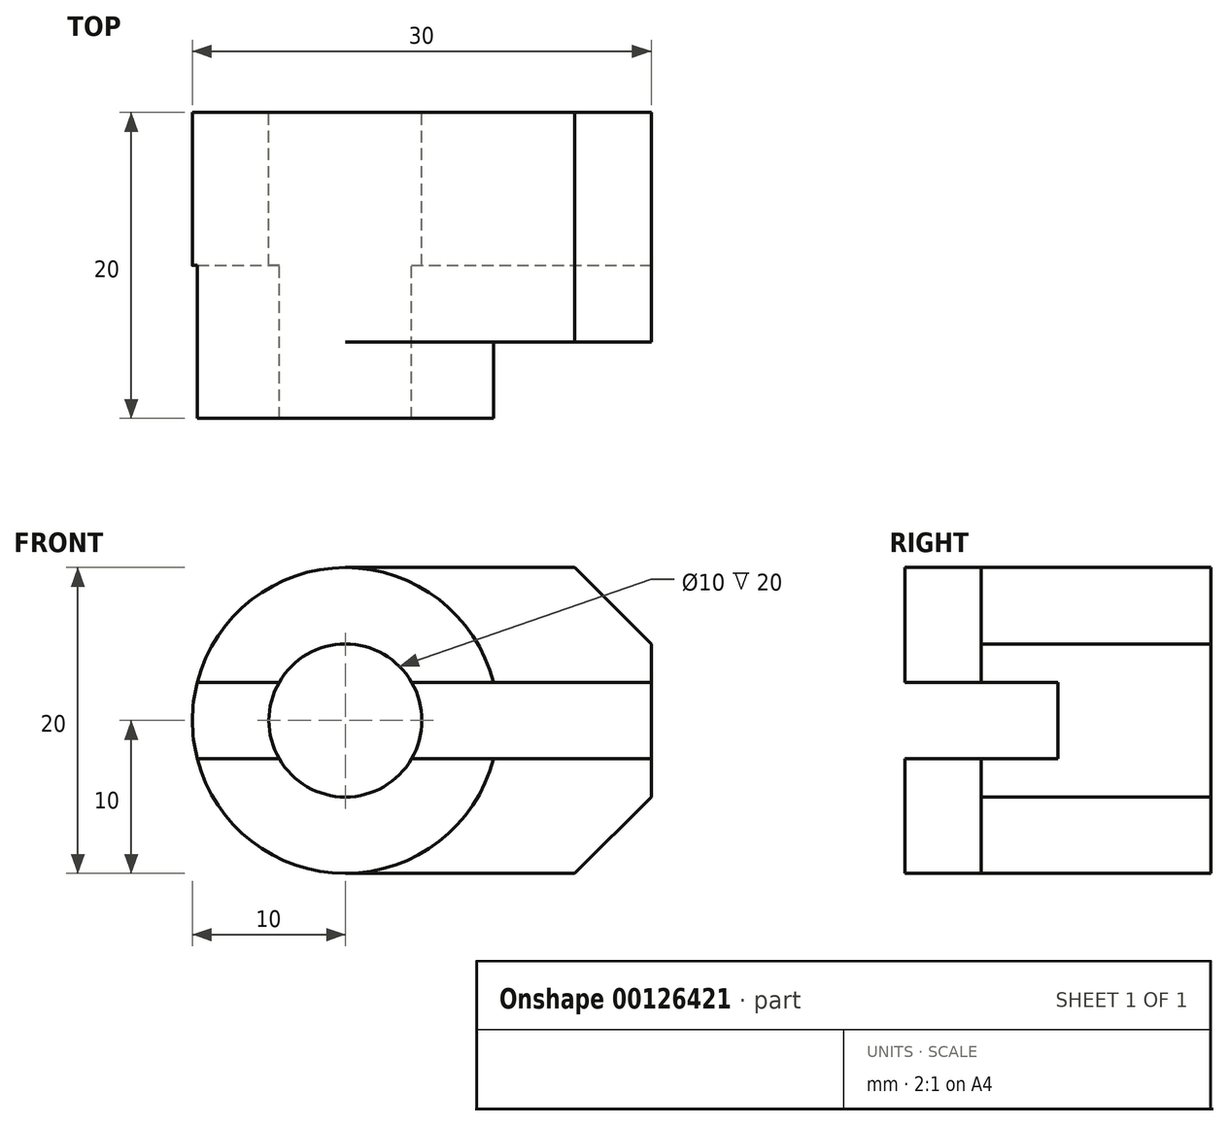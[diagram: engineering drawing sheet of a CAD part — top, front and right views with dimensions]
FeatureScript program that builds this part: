
annotation { "Feature Type Name" : "Feature", "Feature Type Description" : "" }
export const myFeature = defineFeature(function(context is Context, id is Id, definition is map)
    precondition{}
    {
        {
            var Q0;
            Q0=qCreatedBy(makeId("Front.planeOp"),FACE);
            var sketch = newSketch(context, id + "F0", { "sketchPlane" : qUnion([Q0])});
            skCircle(sketch, "E0", {"center": v(0, 0) * mm, "radius": 5 * mm});
            skCircle(sketch, "E1", {"center": v(0, 0) * mm, "radius": 10 * mm});
            skLineSegment(sketch, "E2", {"start": v(0, 10) * mm, "end": v(15, 10) * mm});
            skLineSegment(sketch, "E3", {"start": v(15, 10) * mm, "end": v(20, 5) * mm});
            skLineSegment(sketch, "E4", {"start": v(20, 5) * mm, "end": v(20, -5) * mm});
            skLineSegment(sketch, "E5", {"start": v(20, -5) * mm, "end": v(15, -10) * mm});
            skLineSegment(sketch, "E6", {"start": v(15, -10) * mm, "end": v(0, -10) * mm});
            skSolve(sketch);
        }
        {
            var Q0;
            Q0=makeQuery(id+"F0.imprint","IMPRINT",FACE,{"disambiguationData":[TD([[makeQuery(id+"F0.imprint","IMPRINT",EDGE,{"derivedFrom":sQuery(id+"F0.wireOp",EDGE,"E0")}),-1.0]])]});
            extrude(context, id + "F1", {"entities" : qUnion([Q0]), "depth" : 20 * mm});
        }
        {
            var Q0;
            {var subQ0=sQuery(id+"F0.wireOp",EDGE,"E2");Q0=makeQuery(id+"F0.imprint","IMPRINT",FACE,{"disambiguationData":[TD([[makeQuery(id+"F0.imprint","IMPRINT",EDGE,{"derivedFrom":subQ0}),-1.0]])]});}
            extrude(context, id + "F2", {"entities" : qUnion([Q0]), "operationType" : NewBodyOperationType.ADD, "depth" : 15 * mm});
        }
        {
            var Q0;
            Q0=makeQuery(id+"F2.opExtrude","SWEPT_FACE",FACE,{"disambiguationData":[OSD([sQuery(id+"F0.wireOp",EDGE,"E4")])]});
            var sketch = newSketch(context, id + "F3", { "sketchPlane" : qUnion([Q0])});
            skLineSegment(sketch, "E7", {"start": v(-15, 5) * mm, "end": v(-15, 2.5) * mm, "construction": true});
            skLineSegment(sketch, "E8", {"start": v(-15, 2.5) * mm, "end": v(-15, -2.5) * mm, "construction": true});
            skLineSegment(sketch, "E9", {"start": v(-15, -2.5) * mm, "end": v(-15, -5) * mm, "construction": true});
            skLineSegment(sketch, "E10.bottom", {"start": v(-15, 2.5) * mm, "end": v(-20, 2.5) * mm});
            skLineSegment(sketch, "E10.top", {"start": v(-15, -2.5) * mm, "end": v(-20, -2.5) * mm});
            skLineSegment(sketch, "E10.left", {"start": v(-15, 2.5) * mm, "end": v(-15, -2.5) * mm});
            skLineSegment(sketch, "E10.right", {"start": v(-20, 2.5) * mm, "end": v(-20, -2.5) * mm});
            skLineSegment(sketch, "E11.bottom", {"start": v(-15, 2.5) * mm, "end": v(-10, 2.5) * mm});
            skLineSegment(sketch, "E11.top", {"start": v(-15, -2.5) * mm, "end": v(-10, -2.5) * mm});
            skLineSegment(sketch, "E11.right", {"start": v(-10, 2.5) * mm, "end": v(-10, -2.5) * mm});
            skSolve(sketch);
        }
        {
            var Q0;
            Q0 = qSketchRegion(id + "F3", true);
            extrude(context, id + "F4", {"entities" : qUnion([Q0]), "operationType" : NewBodyOperationType.REMOVE, "endBound" : BoundingType.THROUGH_ALL, "oppositeDirection" : true, "depth" : 25 * mm});
        }
    });
